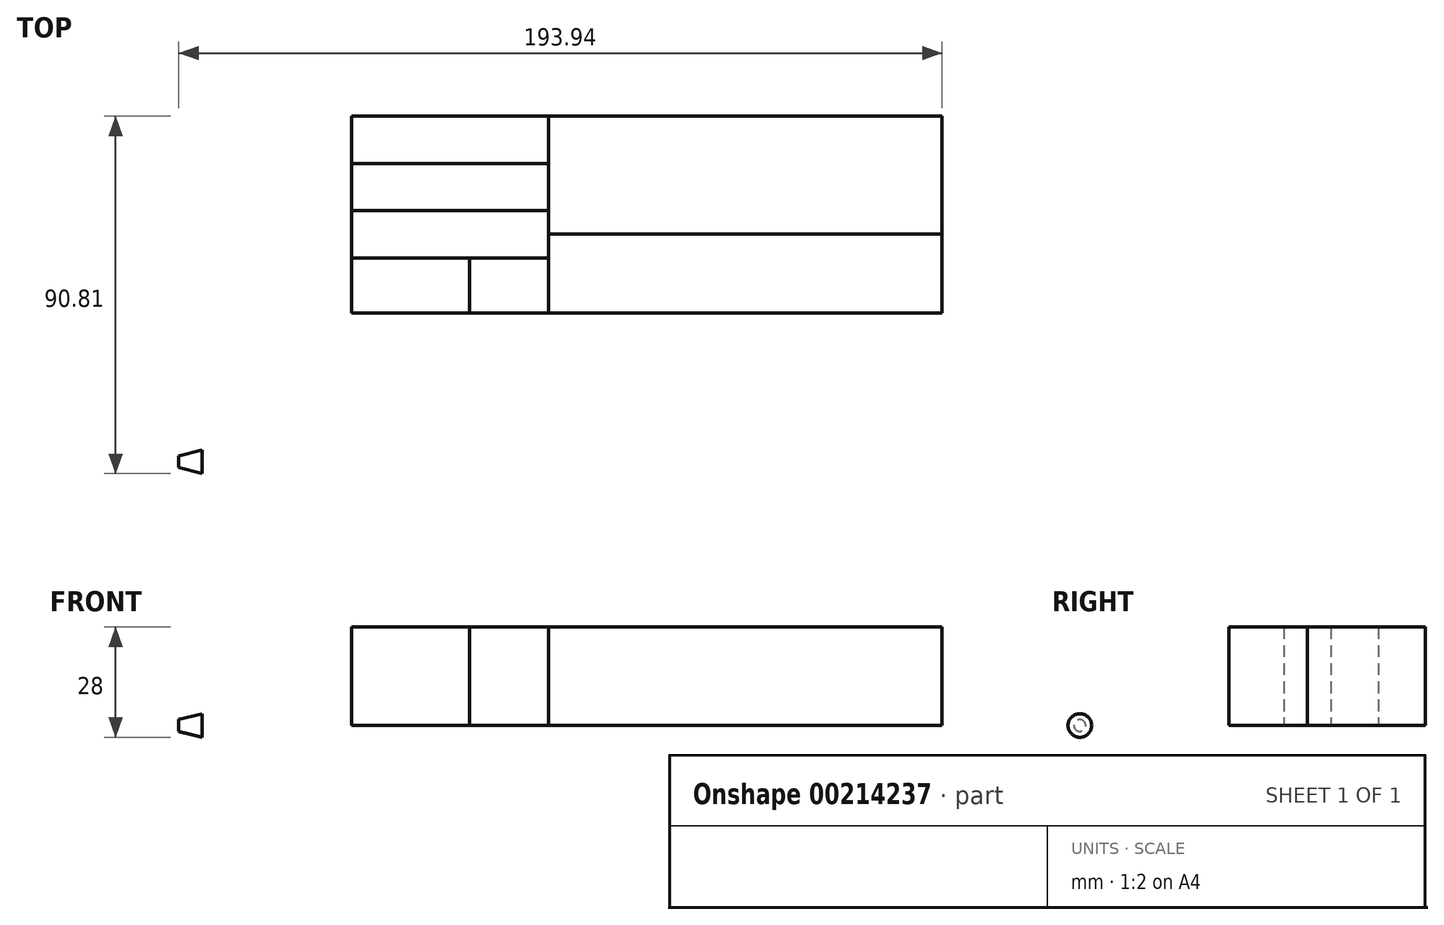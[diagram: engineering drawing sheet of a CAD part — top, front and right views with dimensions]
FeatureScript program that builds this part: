
annotation { "Feature Type Name" : "Feature", "Feature Type Description" : "" }
export const myFeature = defineFeature(function(context is Context, id is Id, definition is map)
    precondition{}
    {
        {
            var Q0;
            Q0=qCreatedBy(makeId("Top.planeOp"),FACE);
            var sketch = newSketch(context, id + "F0", { "sketchPlane" : qUnion([Q0])});
            skLineSegment(sketch, "E0.bottom", {"start": v(0, 0) * mm, "end": v(150, 0) * mm});
            skLineSegment(sketch, "E0.top", {"start": v(0, 50) * mm, "end": v(150, 50) * mm});
            skLineSegment(sketch, "E0.left", {"start": v(0, 0) * mm, "end": v(0, 50) * mm});
            skLineSegment(sketch, "E0.right", {"start": v(150, 0) * mm, "end": v(150, 50) * mm});
            skLineSegment(sketch, "E1", {"start": v(50, 50) * mm, "end": v(50, 0) * mm});
            skLineSegment(sketch, "E2", {"start": v(50, 20) * mm, "end": v(150, 20) * mm});
            skLineSegment(sketch, "E3", {"start": v(0, 38) * mm, "end": v(50, 38) * mm});
            skLineSegment(sketch, "E4", {"start": v(0, 26) * mm, "end": v(50, 26) * mm});
            skLineSegment(sketch, "E5", {"start": v(0, 14) * mm, "end": v(50, 14) * mm});
            skLineSegment(sketch, "E6", {"start": v(30, 14) * mm, "end": v(30, 0) * mm});
            skSolve(sketch);
        }
        {
            var Q0;
            {var subQ5=sQuery(id+"F0.wireOp",EDGE,"E3");Q0=makeQuery(id+"F0.imprint","IMPRINT",FACE,{"disambiguationData":[TD([[makeQuery(id+"F0.imprint","IMPRINT",EDGE,{"derivedFrom":subQ5}),1.0]])]});}
            var Q1;
            {var subQ4=sQuery(id+"F0.wireOp",EDGE,"E4");Q1=makeQuery(id+"F0.imprint","IMPRINT",FACE,{"disambiguationData":[TD([[makeQuery(id+"F0.imprint","IMPRINT",EDGE,{"derivedFrom":subQ4}),-1.0]])]});}
            extrude(context, id + "F1", {"entities" : qUnion([Q0, Q1]), "depth" : 25 * mm, "offsetDistance" : 25 * mm});
        }
        {
            var Q0;
            {var subQ0=sQuery(id+"F0.wireOp",EDGE,"E3");Q0=makeQuery(id+"F0.imprint","IMPRINT",FACE,{"disambiguationData":[TD([[makeQuery(id+"F0.imprint","IMPRINT",EDGE,{"derivedFrom":subQ0}),-1.0]])]});}
            var Q1;
            {var subQ3=sQuery(id+"F0.wireOp",EDGE,"E6");Q1=makeQuery(id+"F0.imprint","IMPRINT",FACE,{"disambiguationData":[TD([[makeQuery(id+"F0.imprint","IMPRINT",EDGE,{"derivedFrom":subQ3}),-1.0]])]});}
            var Q2;
            {var subQ4=sQuery(id+"F0.wireOp",EDGE,"E2");Q2=makeQuery(id+"F0.imprint","IMPRINT",FACE,{"disambiguationData":[TD([[makeQuery(id+"F0.imprint","IMPRINT",EDGE,{"derivedFrom":subQ4}),-1.0]])]});}
            extrude(context, id + "F2", {"entities" : qUnion([Q0, Q1, Q2]), "depth" : 25 * mm, "offsetDistance" : 25 * mm});
        }
        {
            var Q0;
            {var subQ7=sQuery(id+"F0.wireOp",EDGE,"E2");Q0=makeQuery(id+"F0.imprint","IMPRINT",FACE,{"disambiguationData":[TD([[makeQuery(id+"F0.imprint","IMPRINT",EDGE,{"derivedFrom":subQ7}),1.0]])]});}
            var Q1;
            {var subQ3=sQuery(id+"F0.wireOp",EDGE,"E6");Q1=makeQuery(id+"F0.imprint","IMPRINT",FACE,{"disambiguationData":[TD([[makeQuery(id+"F0.imprint","IMPRINT",EDGE,{"derivedFrom":subQ3}),1.0]])]});}
            extrude(context, id + "F3", {"entities" : qUnion([Q0, Q1]), "depth" : 25 * mm, "offsetDistance" : 25 * mm});
        }
        {
            var Q0;
            Q0=qCreatedBy(makeId("Top.planeOp"),FACE);
            var sketch = newSketch(context, id + "F4", { "sketchPlane" : qUnion([Q0])});
            skLineSegment(sketch, "E7", {"start": v(-37.94, -34.8) * mm, "end": v(-37.94, -40.8) * mm});
            skLineSegment(sketch, "E8", {"start": v(-37.94, -37.8) * mm, "end": v(-43.94, -37.8) * mm});
            skLineSegment(sketch, "E9", {"start": v(-43.94, -36.3) * mm, "end": v(-43.94, -39.3) * mm});
            skLineSegment(sketch, "E10", {"start": v(-43.94, -36.3) * mm, "end": v(-37.94, -34.8) * mm});
            skLineSegment(sketch, "E11", {"start": v(-43.94, -39.3) * mm, "end": v(-37.94, -40.8) * mm});
            skSolve(sketch);
        }
        {
            var Q0;
            {var subQ2=sQuery(id+"F4.wireOp",EDGE,"E8");Q0=makeQuery(id+"F4.imprint","IMPRINT",FACE,{"disambiguationData":[TD([[makeQuery(id+"F4.imprint","IMPRINT",EDGE,{"derivedFrom":subQ2}),-1.0]])]});}
            var Q1;
            Q1=sQuery(id+"F4.wireOp",EDGE,"E8");
            revolve(context, id + "F5", {"entities" : qUnion([Q0]), "axis" : qUnion([Q1]), "revolveType" : RevolveType.FULL});
        }
    });
